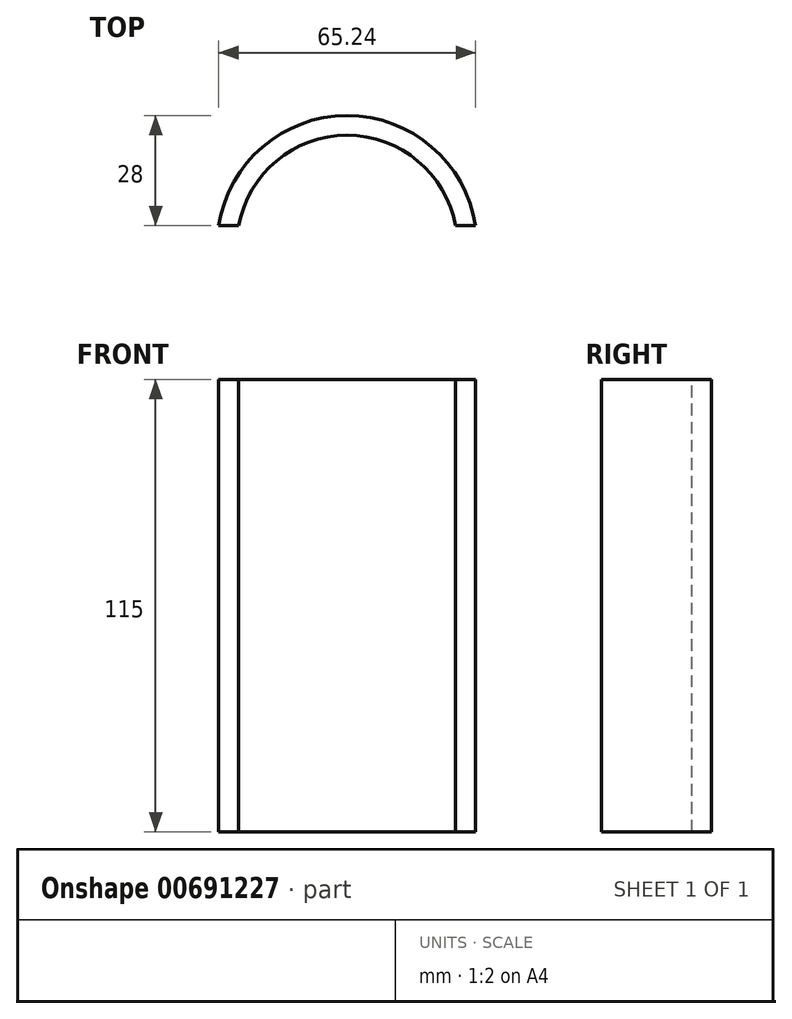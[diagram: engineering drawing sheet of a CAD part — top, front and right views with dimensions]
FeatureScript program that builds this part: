
annotation { "Feature Type Name" : "Feature", "Feature Type Description" : "" }
export const myFeature = defineFeature(function(context is Context, id is Id, definition is map)
    precondition{}
    {
        {
            var Q0;
            Q0=qCreatedBy(makeId("Top.planeOp"),FACE);
            var sketch = newSketch(context, id + "F0", { "sketchPlane" : qUnion([Q0])});
            skArc(sketch, "E0", {"start": v(32.62, 5) * mm, "mid": v(0, 33) * mm, "end": v(-32.62, 5) * mm});
            skArc(sketch, "E1", {"start": v(27.55, 5) * mm, "mid": v(0, 28) * mm, "end": v(-27.55, 5) * mm});
            skLineSegment(sketch, "E2", {"start": v(-32.62, 5) * mm, "end": v(-27.55, 5) * mm});
            skLineSegment(sketch, "E3", {"start": v(27.55, 5) * mm, "end": v(32.62, 5) * mm});
            skSolve(sketch);
        }
        {
            var Q0;
            Q0=makeQuery(id+"F0.imprint","IMPRINT",FACE,{"disambiguationData":[TD([[makeQuery(id+"F0.imprint","IMPRINT",EDGE,{"derivedFrom":sQuery(id+"F0.wireOp",EDGE,"E0")}),1.0]])]});
            extrude(context, id + "F1", {"entities" : qUnion([Q0]), "oppositeDirection" : true, "depth" : 115 * mm});
        }
    });
